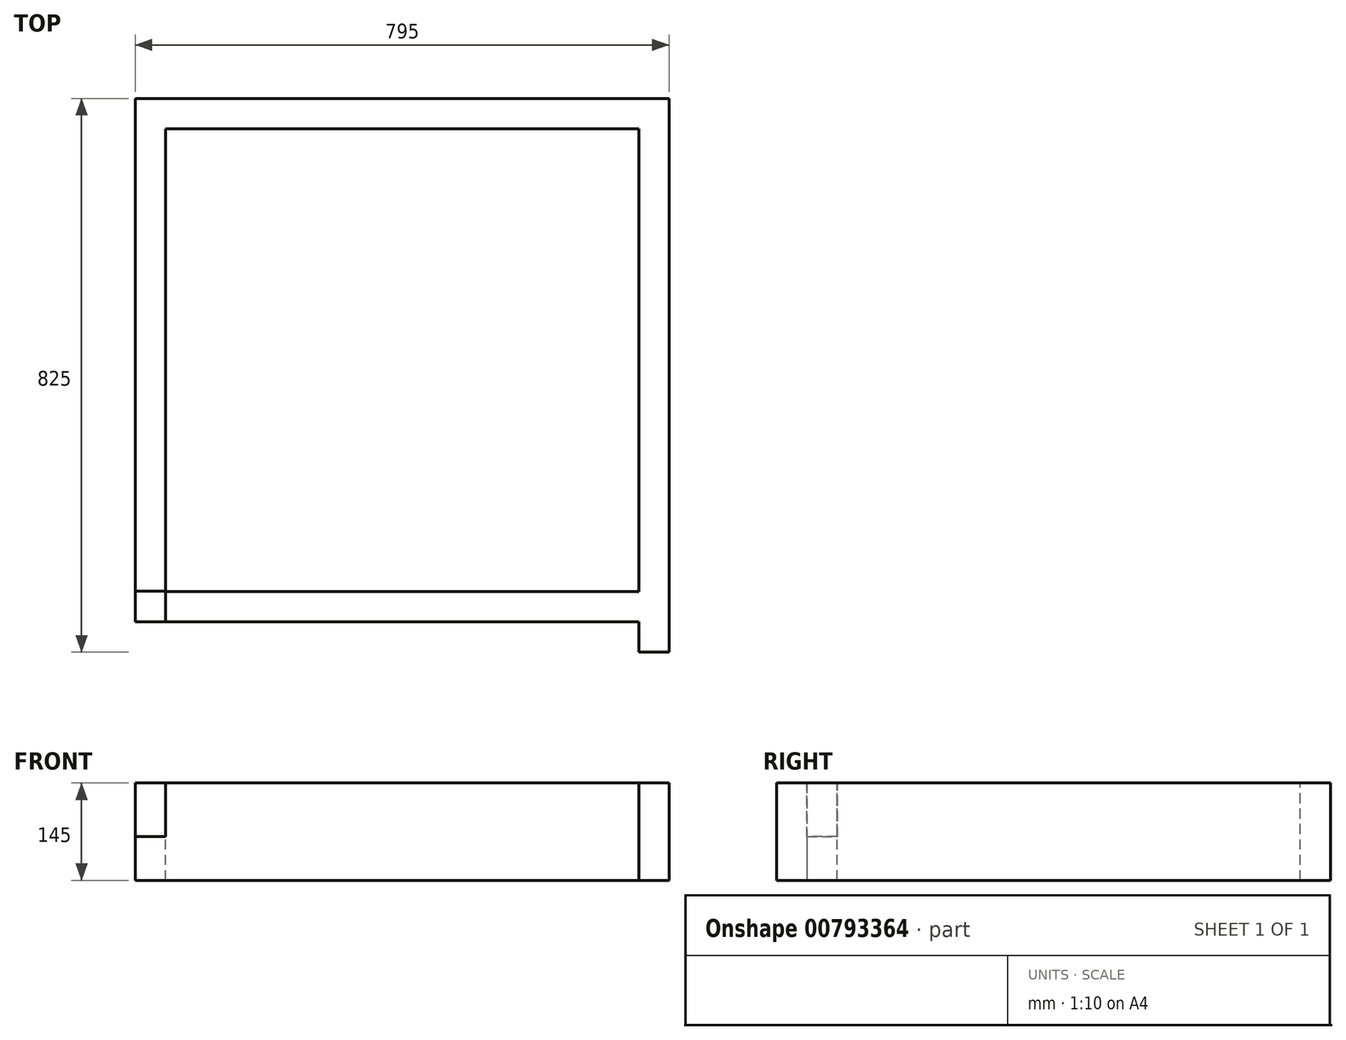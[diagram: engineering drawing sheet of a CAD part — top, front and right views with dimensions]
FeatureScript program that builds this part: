
annotation { "Feature Type Name" : "Feature", "Feature Type Description" : "" }
export const myFeature = defineFeature(function(context is Context, id is Id, definition is map)
    precondition{}
    {
        {
            var Q0;
            Q0=qCreatedBy(makeId("Top.planeOp"),FACE);
            var sketch = newSketch(context, id + "F0", { "sketchPlane" : qUnion([Q0])});
            skLineSegment(sketch, "E0.bottom", {"start": v(-397.5, 390) * mm, "end": v(397.5, 390) * mm});
            skLineSegment(sketch, "E0.top", {"start": v(-397.5, -390) * mm, "end": v(352.5, -390) * mm});
            skLineSegment(sketch, "E0.left", {"start": v(-397.5, 390) * mm, "end": v(-397.5, -390) * mm});
            skLineSegment(sketch, "E0.right", {"start": v(397.5, 390) * mm, "end": v(397.5, -390) * mm});
            skPoint(sketch, "E0.middle", {"position": v(0, 0) * mm});
            skLineSegment(sketch, "E1", {"start": v(352.5, -390) * mm, "end": v(352.5, -435) * mm});
            skLineSegment(sketch, "E2", {"start": v(352.5, -435) * mm, "end": v(397.5, -435) * mm});
            skLineSegment(sketch, "E3", {"start": v(397.5, -435) * mm, "end": v(397.5, -390) * mm});
            skSolve(sketch);
        }
        {
            var Q0;
            Q0=makeQuery(id+"F0.imprint","IMPRINT",FACE,{"disambiguationData":[TD([[makeQuery(id+"F0.imprint","IMPRINT",EDGE,{"derivedFrom":sQuery(id+"F0.wireOp",EDGE,"E0.bottom")}),-1.0]])]});
            extrude(context, id + "F1", {"entities" : qUnion([Q0]), "depth" : 145 * mm, "offsetDistance" : 25 * mm});
        }
        {
            var Q0;
            Q0=makeQuery(id+"F1.opExtrude","CAP_FACE",FACE,{"disambiguationData":[OSD([sQuery(id+"F0.wireOp",EDGE,"E0.bottom"),sQuery(id+"F0.wireOp",EDGE,"E0.top"),sQuery(id+"F0.wireOp",EDGE,"E0.left"),sQuery(id+"F0.wireOp",EDGE,"E0.right"),sQuery(id+"F0.wireOp",EDGE,"E1"),sQuery(id+"F0.wireOp",EDGE,"E2"),sQuery(id+"F0.wireOp",EDGE,"E3")])],"isStart":false});
            var sketch = newSketch(context, id + "F2", { "sketchPlane" : qUnion([Q0])});
            skLineSegment(sketch, "E4.bottom", {"start": v(-352.5, -345) * mm, "end": v(352.5, -345) * mm});
            skLineSegment(sketch, "E4.top", {"start": v(-352.5, 345) * mm, "end": v(352.5, 345) * mm});
            skLineSegment(sketch, "E4.left", {"start": v(-352.5, -345) * mm, "end": v(-352.5, 345) * mm});
            skLineSegment(sketch, "E4.right", {"start": v(352.5, -345) * mm, "end": v(352.5, 345) * mm});
            skSolve(sketch);
        }
        {
            var Q0;
            Q0 = qSketchRegion(id + "F2", true);
            extrude(context, id + "F3", {"entities" : qUnion([Q0]), "operationType" : NewBodyOperationType.REMOVE, "endBound" : BoundingType.THROUGH_ALL, "oppositeDirection" : true, "depth" : 25 * mm, "offsetDistance" : 25 * mm});
        }
        {
            var Q0;
            Q0=makeQuery(id+"F1.opExtrude","CAP_FACE",FACE,{"disambiguationData":[OSD([sQuery(id+"F0.wireOp",EDGE,"E0.bottom"),sQuery(id+"F0.wireOp",EDGE,"E0.top"),sQuery(id+"F0.wireOp",EDGE,"E0.left"),sQuery(id+"F0.wireOp",EDGE,"E0.right"),sQuery(id+"F0.wireOp",EDGE,"E1"),sQuery(id+"F0.wireOp",EDGE,"E2"),sQuery(id+"F0.wireOp",EDGE,"E3")])],"isStart":false});
            var sketch = newSketch(context, id + "F4", { "sketchPlane" : qUnion([Q0])});
            skLineSegment(sketch, "E5.bottom", {"start": v(-397.5, -390) * mm, "end": v(-352.5, -390) * mm});
            skLineSegment(sketch, "E5.top", {"start": v(-397.5, -344) * mm, "end": v(-352.5, -344) * mm});
            skLineSegment(sketch, "E5.left", {"start": v(-397.5, -390) * mm, "end": v(-397.5, -344) * mm});
            skLineSegment(sketch, "E5.right", {"start": v(-352.5, -390) * mm, "end": v(-352.5, -344) * mm});
            skSolve(sketch);
        }
        {
            var Q0;
            {var subQ3=sQuery(id+"F4.wireOp",EDGE,"E5.bottom");Q0=makeQuery(id+"F4.imprint","IMPRINT",FACE,{"disambiguationData":[TD([[makeQuery(id+"F4.imprint","IMPRINT",EDGE,{"derivedFrom":subQ3}),1.0]])]});}
            extrude(context, id + "F5", {"entities" : qUnion([Q0]), "operationType" : NewBodyOperationType.REMOVE, "oppositeDirection" : true, "depth" : 80 * mm, "offsetDistance" : 25 * mm});
        }
    });
